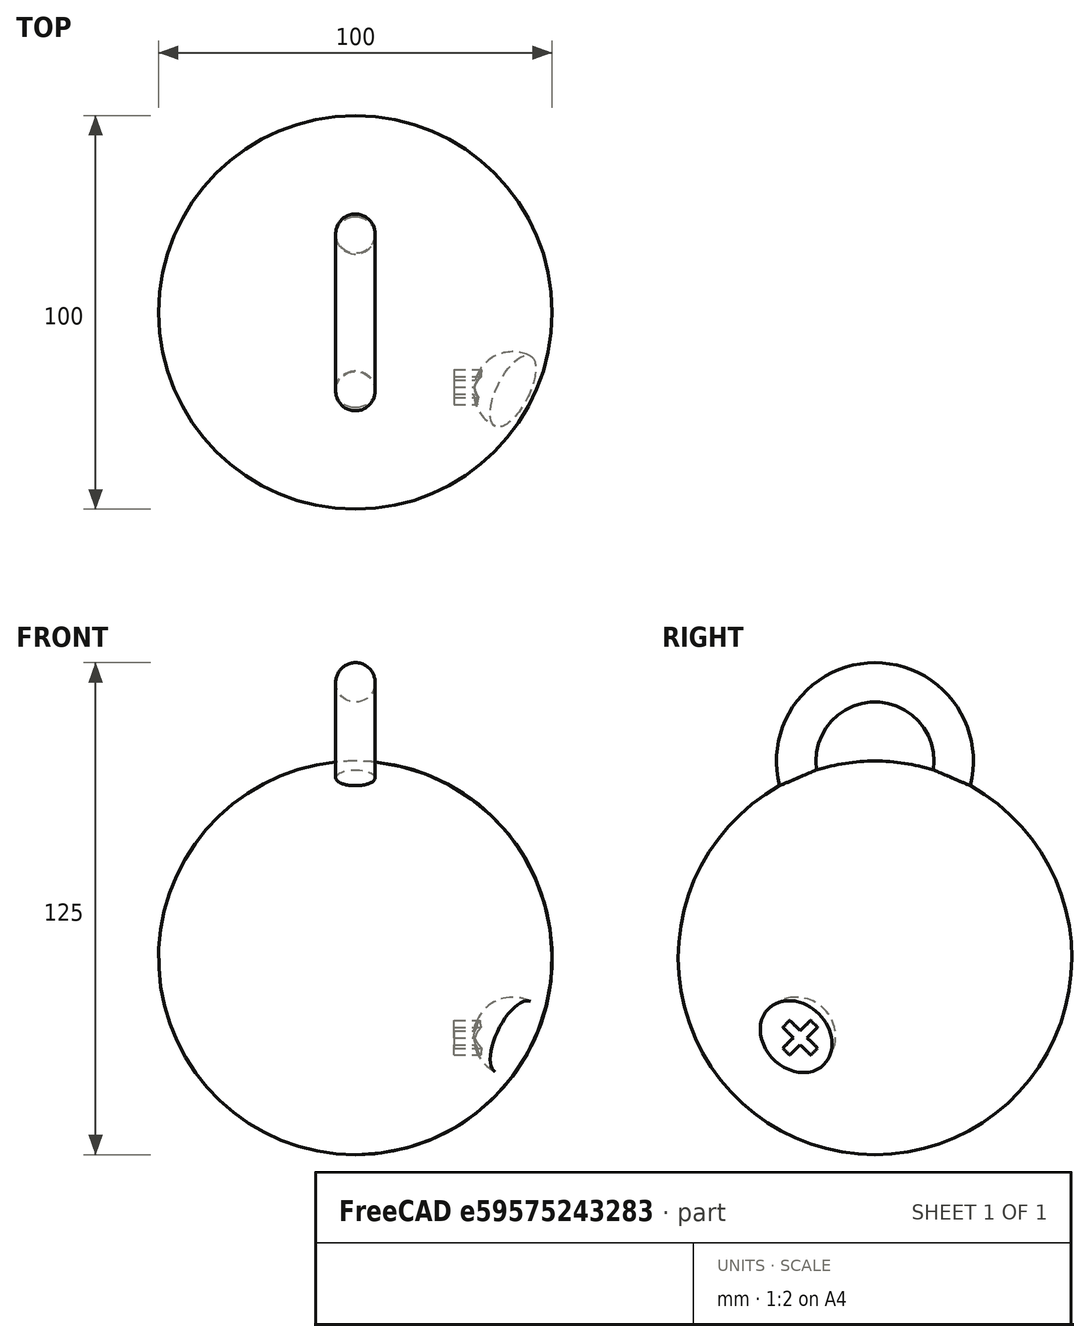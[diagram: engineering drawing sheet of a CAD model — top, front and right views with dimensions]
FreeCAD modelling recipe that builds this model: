
FCSTD DOCUMENT  (FreeCAD 0.16R6703 (Git))
Label: portecleventremoucreux
License: All rights reserved
LicenseURL: http://en.wikipedia.org/wiki/All_rights_reserved
objects: Part::Cut×3, Part::Sphere×2, Part::Box×2, Part::Torus×1, Part::MultiFuse×1
note: 9 computed .brp shape members not serialized (recipe doc carries the construction recipe); baked Part::Feature solids carry a one-line shape summary decoded from their .brp

FEATURE [Part::Sphere] Sphere  label="Sphère"
  Angle1 = -90
  Angle2 = 90
  Angle3 = 360
  Radius = 50
FEATURE [Part::Sphere] Sphere001  label="Sphère001"
  Angle1 = -90
  Angle2 = 90
  Angle3 = 360
  Placement = pos=(40,-20,-20) rot=(0,0,1;0rad)
  Radius = 10
FEATURE [Part::Box] Box  label="Boîte"
  Height = 10
  Length = 10
  Placement = pos=(25,-16.3483,-24.7037) rot=(1,0,0;0.785398rad)
  Width = 2.5
FEATURE [Part::Box] Box001  label="Boîte001"
  Height = 10
  Length = 10
  Placement = pos=(25,-14.5806,-17.6326) rot=(1,0,0;2.35619rad)
  Width = 2.5
FEATURE [Part::Torus] Torus  label="Tore"
  Angle1 = -180
  Angle2 = 180
  Angle3 = 360
  Placement = pos=(0,0,50) rot=(0,1,0;1.5708rad)
  Radius1 = 20
  Radius2 = 5
FEATURE [Part::Cut] Cut
  Base = -> Sphere
  Tool = -> Sphere001
FEATURE [Part::MultiFuse] Fusion
  Shapes = -> [Cut,Torus]
FEATURE [Part::Cut] Cut001
  Base = -> Fusion
  Tool = -> Box
FEATURE [Part::Cut] Cut002
  Base = -> Cut001
  Tool = -> Box001
